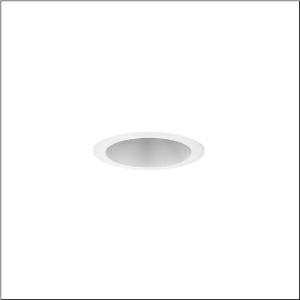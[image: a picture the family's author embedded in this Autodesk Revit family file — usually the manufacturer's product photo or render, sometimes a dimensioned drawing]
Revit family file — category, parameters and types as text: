
# Revit family: lunis_31_mini_51dn167e41
name_source: partatom
category: Lighting Fixtures
units: mm (PartAtom-declared; Revit-internal decimal feet)

## family parameters
Cut with Voids When Loaded = No
Host = Face
Light Source = No
Part Type = Normal
Room Calculation Point = No
Round Connector Dimension = Use Diameter
Shared = No

## types (1)
- Lunis 31 mini (1 x LED, 1040 lm, 8.3 W, 4000K)
    Apparent Load = 8 VA
    CIE Flux Codes = 69 93 99 100 100
    Color Rendering = 80
    Color Temperature = 4000K
    Default Elevation = 1800 mm
    Description = Lunis 31,  mini, downlight, light control with reflector, light emission: direct distribution, LED rated luminous flux: 1.040lm, light colour: 840, mains connection: 220..240V, AC, 50/60Hz, housing, white, protection rating (complete): IP20, protection rating (on room side): IP54, insulation class (complete): insulation class II (safety insulation), certification: CE, packaging unit: 1 piece
    Height = 0 mm  [stored 0 ft]
    Lamp = 1 x LED
    Lamp Light Flux = 1040 lm
    Lamp Power = 8.3 W
    Lamp count = 1
    Length = 188 mm  [stored 0.616798 ft]
    Luminous efficacy = 125 lm/W
    Manufacturer = Siteco
    ModVariant = No
    Model = 51DN167E41
    Mounting Place = Ceiling
    Mounting Type = Recessed
    Number of Poles = 1
    OnlyDefault = Yes
    Power Factor = 1
    Product Name = Lunis 31 mini
    Product group = downlight
    ProductGroupID = 400
    Protection Class = Protection class II
    Protection Degree = IP 20
    RLX_Detail_Level = 1
    RLX_Emergency_Light_Flux = 0 lm
    RLX_Emergency_Type = 0
    RLX_Emergency_Type_DB = No
    RlxData = <blob elided: 21721 chars, md5=52b33307>
    Socket = socket
    Standby Power = 0 W
    System Light Flux = 1040 lm
    System Power = 8 W
    Type Comments = Product without accessories
    Type Image = l_1005624.jpg
    URL = http://relux.com
    VarID = ---
    Voltage = 0 V
    Weight = 0.00 kg
    Width = 0 mm  [stored 0 ft]

note: [stored X ft] marks values corroborated as IEEE doubles in the binary element streams (Revit-internal decimal feet)

## geometry (parser evidence)
native form markers: Blend x4, Sweep x10
no freeform markers — native parametric forms only
